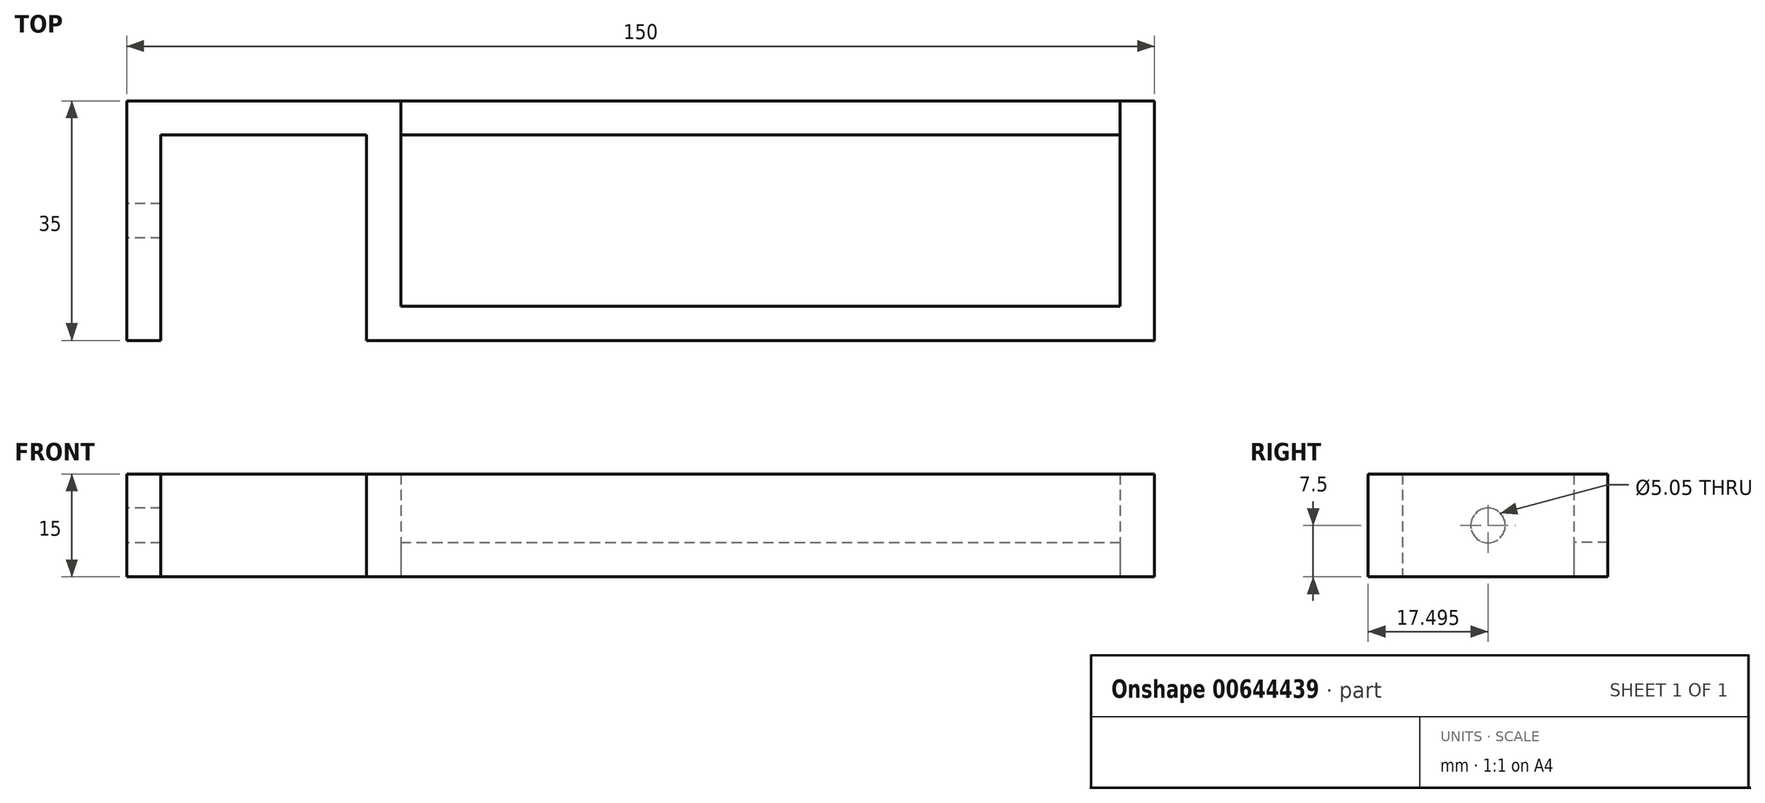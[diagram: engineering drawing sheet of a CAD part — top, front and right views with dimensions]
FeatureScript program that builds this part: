
annotation { "Feature Type Name" : "Feature", "Feature Type Description" : "" }
export const myFeature = defineFeature(function(context is Context, id is Id, definition is map)
    precondition{}
    {
        {
            var Q0;
            Q0=qCreatedBy(makeId("Top.planeOp"),FACE);
            var sketch = newSketch(context, id + "F0", { "sketchPlane" : qUnion([Q0])});
            skLineSegment(sketch, "E0.bottom", {"start": v(-56.22, -19.83) * mm, "end": v(48.78, -19.83) * mm});
            skLineSegment(sketch, "E0.top", {"start": v(-56.22, -44.83) * mm, "end": v(48.78, -44.83) * mm});
            skLineSegment(sketch, "E0.left", {"start": v(-56.22, -19.83) * mm, "end": v(-56.22, -44.83) * mm});
            skLineSegment(sketch, "E0.right", {"start": v(48.78, -19.83) * mm, "end": v(48.78, -44.83) * mm});
            skLineSegment(sketch, "E1.0", {"start": v(-61.22, -14.83) * mm, "end": v(-61.22, -49.83) * mm});
            skLineSegment(sketch, "E1.1", {"start": v(-61.22, -14.83) * mm, "end": v(53.78, -14.83) * mm});
            skLineSegment(sketch, "E1.2", {"start": v(53.78, -14.83) * mm, "end": v(53.78, -49.83) * mm});
            skLineSegment(sketch, "E1.3", {"start": v(-61.22, -49.83) * mm, "end": v(53.78, -49.83) * mm});
            skLineSegment(sketch, "E2", {"start": v(-61.22, -14.83) * mm, "end": v(-96.22, -14.83) * mm});
            skLineSegment(sketch, "E3", {"start": v(-96.22, -14.83) * mm, "end": v(-96.22, -49.83) * mm});
            skLineSegment(sketch, "E4.0", {"start": v(-91.22, -19.83) * mm, "end": v(-91.22, -49.83) * mm});
            skLineSegment(sketch, "E4.1", {"start": v(-61.22, -19.83) * mm, "end": v(-91.22, -19.83) * mm});
            skLineSegment(sketch, "E5", {"start": v(-91.22, -49.83) * mm, "end": v(-96.22, -49.83) * mm});
            skSolve(sketch);
        }
        {
            var Q0;
            {var subQ0=sQuery(id+"F0.wireOp",EDGE,"E2");Q0=makeQuery(id+"F0.imprint","IMPRINT",FACE,{"disambiguationData":[TD([[makeQuery(id+"F0.imprint","IMPRINT",EDGE,{"derivedFrom":subQ0}),1.0]])]});}
            var Q1;
            Q1=makeQuery(id+"F0.imprint","IMPRINT",FACE,{"disambiguationData":[TD([[makeQuery(id+"F0.imprint","IMPRINT",EDGE,{"derivedFrom":sQuery(id+"F0.wireOp",EDGE,"E0.bottom")}),1.0]])]});
            extrude(context, id + "F1", {"entities" : qUnion([Q0, Q1]), "depth" : 15 * mm, "offsetDistance" : 25 * mm});
        }
        {
            var Q0;
            Q0=makeQuery(id+"F1.opExtrude","SWEPT_FACE",FACE,{"disambiguationData":[OSD([sQuery(id+"F0.wireOp",EDGE,"E3")])]});
            var sketch = newSketch(context, id + "F2", { "sketchPlane" : qUnion([Q0])});
            skCircle(sketch, "E6", {"center": v(32.33, 7.5) * mm, "radius": 2.52 * mm});
            skSolve(sketch);
        }
        {
            var Q0;
            Q0=makeQuery(id+"F2.imprint","IMPRINT",FACE,{"disambiguationData":[TD([[makeQuery(id+"F2.imprint","IMPRINT",EDGE,{"derivedFrom":sQuery(id+"F2.wireOp",EDGE,"E6")}),1.0]])]});
            extrude(context, id + "F3", {"entities" : qUnion([Q0]), "operationType" : NewBodyOperationType.REMOVE, "oppositeDirection" : true, "depth" : 25 * mm, "offsetDistance" : 25 * mm});
        }
        {
            var Q0;
            Q0=makeQuery(id+"F1.opExtrude","SWEPT_FACE",FACE,{"disambiguationData":[OSD([sQuery(id+"F0.wireOp",EDGE,"E0.bottom")])]});
            var sketch = newSketch(context, id + "F4", { "sketchPlane" : qUnion([Q0])});
            skLineSegment(sketch, "E7", {"start": v(-56.22, 15) * mm, "end": v(-56.22, 0) * mm});
            skLineSegment(sketch, "E8", {"start": v(48.78, 0) * mm, "end": v(48.78, 15) * mm});
            skLineSegment(sketch, "E9.bottom", {"start": v(-56.22, 5) * mm, "end": v(48.78, 5) * mm});
            skLineSegment(sketch, "E9.top", {"start": v(-56.22, 10) * mm, "end": v(48.78, 10) * mm});
            skLineSegment(sketch, "E9.left", {"start": v(-56.22, 5) * mm, "end": v(-56.22, 10) * mm});
            skLineSegment(sketch, "E9.right", {"start": v(48.78, 5) * mm, "end": v(48.78, 10) * mm});
            skSolve(sketch);
        }
        {
            var Q0;
            {var subQ2=sQuery(id+"F4.wireOp",EDGE,"E9.top");Q0=makeQuery(id+"F4.imprint","IMPRINT",FACE,{"disambiguationData":[TD([[makeQuery(id+"F4.imprint","IMPRINT",EDGE,{"derivedFrom":subQ2}),1.0]])]});}
            var Q1;
            Q1=makeQuery(id+"F4.imprint","IMPRINT",FACE,{"disambiguationData":[TD([[makeQuery(id+"F4.imprint","IMPRINT",EDGE,{"derivedFrom":sQuery(id+"F4.wireOp",EDGE,"E9.bottom")}),1.0]])]});
            extrude(context, id + "F5", {"entities" : qUnion([Q0, Q1]), "operationType" : NewBodyOperationType.REMOVE, "oppositeDirection" : true, "depth" : 25 * mm, "offsetDistance" : 25 * mm});
        }
    });
